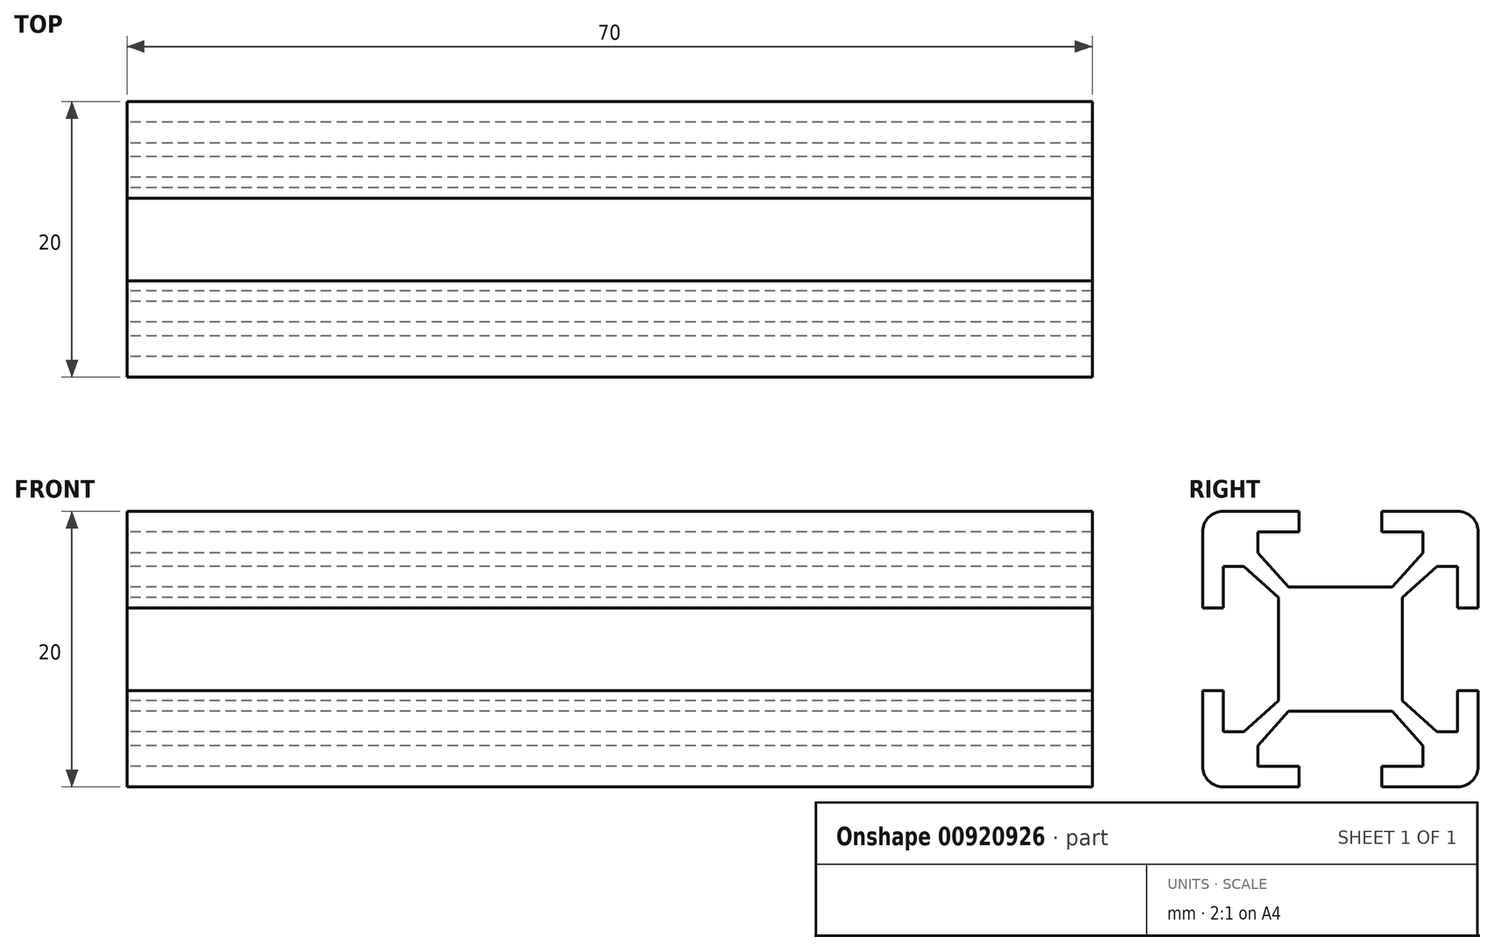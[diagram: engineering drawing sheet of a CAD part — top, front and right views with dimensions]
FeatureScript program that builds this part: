
annotation { "Feature Type Name" : "Feature", "Feature Type Description" : "" }
export const myFeature = defineFeature(function(context is Context, id is Id, definition is map)
    precondition{}
    {
        {
            var Q0;
            Q0=qCreatedBy(makeId("Right.planeOp"),FACE);
            var sketch = newSketch(context, id + "F0", { "sketchPlane" : qUnion([Q0])});
            skLineSegment(sketch, "E0.bottom", {"start": v(8.5, 10) * mm, "end": v(3, 10) * mm});
            skLineSegment(sketch, "E0.top", {"start": v(8.5, -10) * mm, "end": v(-8.5, -10) * mm});
            skLineSegment(sketch, "E0.left", {"start": v(10, 8.5) * mm, "end": v(10, 3) * mm});
            skLineSegment(sketch, "E0.right", {"start": v(-10, 8.5) * mm, "end": v(-10, 3) * mm});
            skPoint(sketch, "E0.middle", {"position": v(0, 0) * mm});
            skPoint(sketch, "E1.visualSharp", {"position": v(-10, 10) * mm});
            skArc(sketch, "E1.filletArc", {"start": v(-8.5, 10) * mm, "mid": v(-9.56, 9.56) * mm, "end": v(-10, 8.5) * mm});
            skPoint(sketch, "E2.visualSharp", {"position": v(10, 10) * mm});
            skArc(sketch, "E2.filletArc", {"start": v(10, 8.5) * mm, "mid": v(9.56, 9.56) * mm, "end": v(8.5, 10) * mm});
            skPoint(sketch, "E3.visualSharp", {"position": v(10, -10) * mm});
            skArc(sketch, "E3.filletArc", {"start": v(8.5, -10) * mm, "mid": v(9.56, -9.56) * mm, "end": v(10, -8.5) * mm});
            skPoint(sketch, "E4.visualSharp", {"position": v(-10, -10) * mm});
            skArc(sketch, "E4.filletArc", {"start": v(-10, -8.5) * mm, "mid": v(-9.56, -9.56) * mm, "end": v(-8.5, -10) * mm});
            skLineSegment(sketch, "E5", {"start": v(-3, 10) * mm, "end": v(-3, 8.5) * mm});
            skLineSegment(sketch, "E6", {"start": v(-3, 8.5) * mm, "end": v(-6, 8.5) * mm});
            skLineSegment(sketch, "E7", {"start": v(-6, 8.5) * mm, "end": v(-6, 7) * mm});
            skLineSegment(sketch, "E8", {"start": v(-6, 7) * mm, "end": v(-3.75, 4.5) * mm});
            skLineSegment(sketch, "E9", {"start": v(-3.75, 4.5) * mm, "end": v(0, 4.5) * mm});
            skLineSegment(sketch, "E10.MirrorCS", {"start": v(3, 10) * mm, "end": v(3, 8.5) * mm});
            skLineSegment(sketch, "E11.MirrorCS", {"start": v(3, 8.5) * mm, "end": v(6, 8.5) * mm});
            skLineSegment(sketch, "E12.MirrorCS", {"start": v(6, 8.5) * mm, "end": v(6, 7) * mm});
            skLineSegment(sketch, "E13.MirrorCS", {"start": v(6, 7) * mm, "end": v(3.75, 4.5) * mm});
            skLineSegment(sketch, "E14.MirrorCS", {"start": v(3.75, 4.5) * mm, "end": v(0, 4.5) * mm});
            skLineSegment(sketch, "E15.trimOffspring", {"start": v(-3, 10) * mm, "end": v(-8.5, 10) * mm});
            skLineSegment(sketch, "E16.1.0", {"start": v(-8.5, -3) * mm, "end": v(-8.5, -6) * mm});
            skLineSegment(sketch, "E16.1.1", {"start": v(-8.5, -6) * mm, "end": v(-7, -6) * mm});
            skLineSegment(sketch, "E16.1.2", {"start": v(-7, -6) * mm, "end": v(-4.5, -3.75) * mm});
            skLineSegment(sketch, "E16.1.3", {"start": v(-4.5, -3.75) * mm, "end": v(-4.5, 0) * mm});
            skLineSegment(sketch, "E16.1.4", {"start": v(-4.5, 3.75) * mm, "end": v(-4.5, 0) * mm});
            skLineSegment(sketch, "E16.1.5", {"start": v(-7, 6) * mm, "end": v(-4.5, 3.75) * mm});
            skLineSegment(sketch, "E16.1.6", {"start": v(-8.5, 6) * mm, "end": v(-7, 6) * mm});
            skLineSegment(sketch, "E16.1.7", {"start": v(-8.5, 3) * mm, "end": v(-8.5, 6) * mm});
            skLineSegment(sketch, "E16.1.8", {"start": v(-10, 3) * mm, "end": v(-8.5, 3) * mm});
            skLineSegment(sketch, "E16.1.9", {"start": v(-10, -3) * mm, "end": v(-8.5, -3) * mm});
            skLineSegment(sketch, "E16.2.0", {"start": v(3, -8.5) * mm, "end": v(6, -8.5) * mm});
            skLineSegment(sketch, "E16.2.1", {"start": v(6, -8.5) * mm, "end": v(6, -7) * mm});
            skLineSegment(sketch, "E16.2.2", {"start": v(6, -7) * mm, "end": v(3.75, -4.5) * mm});
            skLineSegment(sketch, "E16.2.3", {"start": v(3.75, -4.5) * mm, "end": v(0, -4.5) * mm});
            skLineSegment(sketch, "E16.2.4", {"start": v(-3.75, -4.5) * mm, "end": v(0, -4.5) * mm});
            skLineSegment(sketch, "E16.2.5", {"start": v(-6, -7) * mm, "end": v(-3.75, -4.5) * mm});
            skLineSegment(sketch, "E16.2.6", {"start": v(-6, -8.5) * mm, "end": v(-6, -7) * mm});
            skLineSegment(sketch, "E16.2.7", {"start": v(-3, -8.5) * mm, "end": v(-6, -8.5) * mm});
            skLineSegment(sketch, "E16.2.8", {"start": v(-3, -10) * mm, "end": v(-3, -8.5) * mm});
            skLineSegment(sketch, "E16.2.9", {"start": v(3, -10) * mm, "end": v(3, -8.5) * mm});
            skLineSegment(sketch, "E16.3.0", {"start": v(8.5, 3) * mm, "end": v(8.5, 6) * mm});
            skLineSegment(sketch, "E16.3.1", {"start": v(8.5, 6) * mm, "end": v(7, 6) * mm});
            skLineSegment(sketch, "E16.3.2", {"start": v(7, 6) * mm, "end": v(4.5, 3.75) * mm});
            skLineSegment(sketch, "E16.3.3", {"start": v(4.5, 3.75) * mm, "end": v(4.5, 0) * mm});
            skLineSegment(sketch, "E16.3.4", {"start": v(4.5, -3.75) * mm, "end": v(4.5, 0) * mm});
            skLineSegment(sketch, "E16.3.5", {"start": v(7, -6) * mm, "end": v(4.5, -3.75) * mm});
            skLineSegment(sketch, "E16.3.6", {"start": v(8.5, -6) * mm, "end": v(7, -6) * mm});
            skLineSegment(sketch, "E16.3.7", {"start": v(8.5, -3) * mm, "end": v(8.5, -6) * mm});
            skLineSegment(sketch, "E16.3.8", {"start": v(10, -3) * mm, "end": v(8.5, -3) * mm});
            skLineSegment(sketch, "E16.3.9", {"start": v(10, 3) * mm, "end": v(8.5, 3) * mm});
            skLineSegment(sketch, "E17.trimOffspring", {"start": v(-10, -3) * mm, "end": v(-10, -8.5) * mm});
            skLineSegment(sketch, "E18.trimOffspring", {"start": v(10, -3) * mm, "end": v(10, -8.5) * mm});
            skSolve(sketch);
        }
        {
            var Q0;
            Q0=makeQuery(id+"F0.imprint","IMPRINT",FACE,{"disambiguationData":[TD([[makeQuery(id+"F0.imprint","IMPRINT",EDGE,{"derivedFrom":sQuery(id+"F0.wireOp",EDGE,"E0.bottom")}),1.0]])]});
            extrude(context, id + "F1", {"entities" : qUnion([Q0]), "depth" : 70 * mm, "offsetDistance" : 25 * mm});
        }
    });
